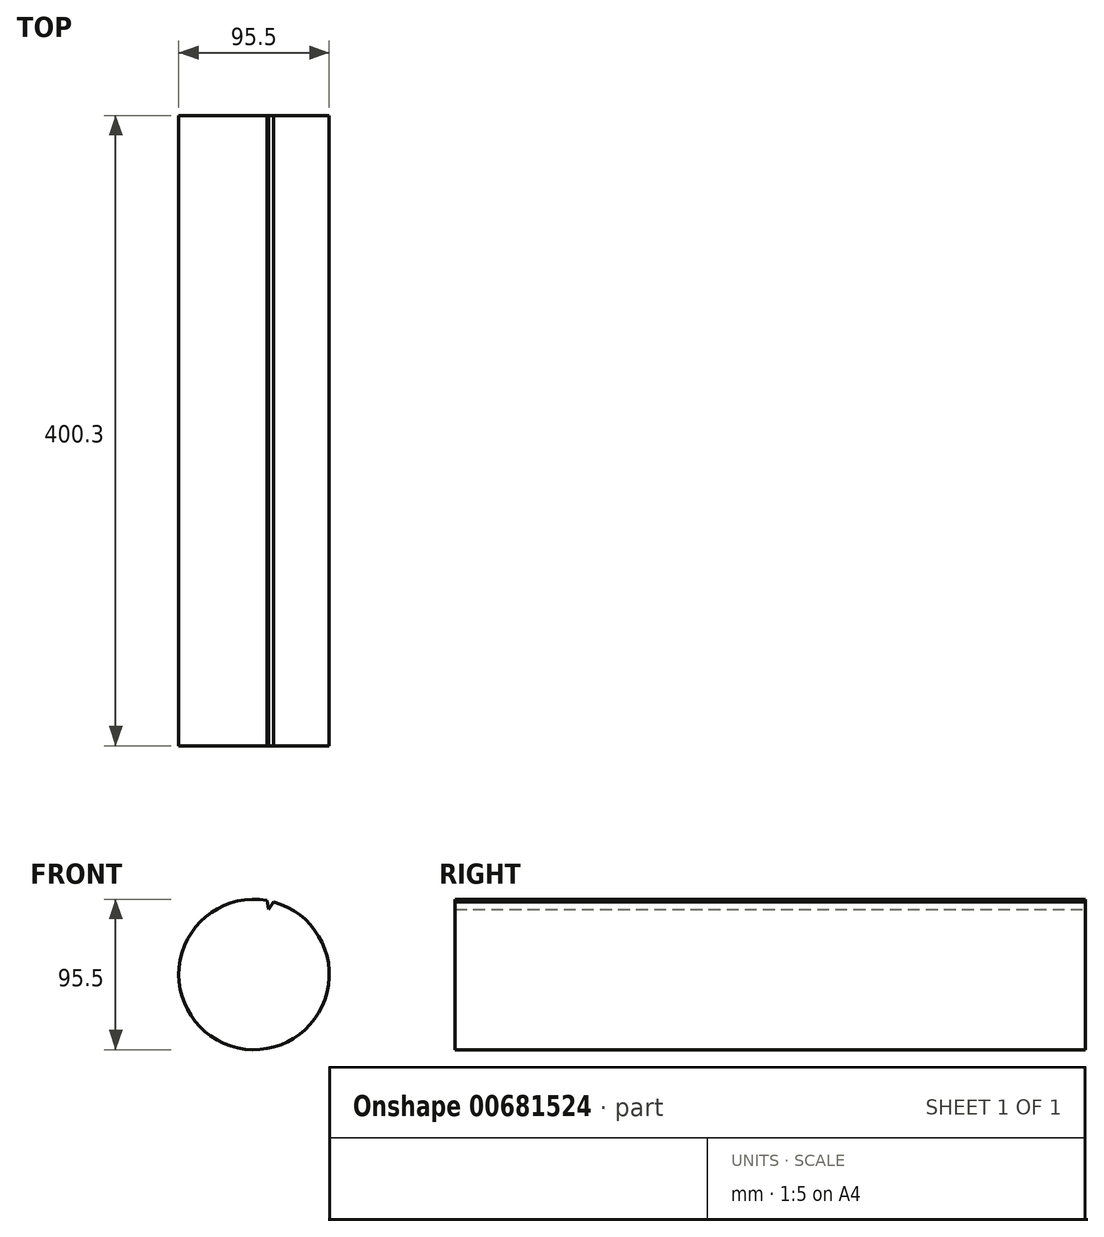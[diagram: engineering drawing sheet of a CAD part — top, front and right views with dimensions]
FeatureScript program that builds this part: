
annotation { "Feature Type Name" : "Feature", "Feature Type Description" : "" }
export const myFeature = defineFeature(function(context is Context, id is Id, definition is map)
    precondition{}
    {
        {
            var Q0;
            Q0=qCreatedBy(makeId("Front.planeOp"),FACE);
            var sketch = newSketch(context, id + "F0", { "sketchPlane" : qUnion([Q0])});
            skCircle(sketch, "E0", {"center": v(0, 0) * mm, "radius": 47.75 * mm});
            skSolve(sketch);
        }
        {
            var Q0;
            Q0=makeQuery(id+"F0.imprint","IMPRINT",FACE,{"disambiguationData":[TD([[makeQuery(id+"F0.imprint","IMPRINT",EDGE,{"derivedFrom":sQuery(id+"F0.wireOp",EDGE,"E0")}),1.0]])]});
            extrude(context, id + "F1", {"entities" : qUnion([Q0]), "depth" : 400.3 * mm, "offsetDistance" : 25.4 * mm});
        }
        {
            var Q0;
            Q0=makeQuery(id+"F1.opExtrude","CAP_FACE",FACE,{"disambiguationData":[OSD([sQuery(id+"F0.wireOp",EDGE,"E0")])],"isStart":true});
            var sketch = newSketch(context, id + "F2", { "sketchPlane" : qUnion([Q0])});
            skLineSegment(sketch, "E1", {"start": v(-6.71, 56.6) * mm, "end": v(-9.17, 41.4) * mm});
            skLineSegment(sketch, "E2", {"start": v(-9.17, 41.4) * mm, "end": v(-17.8, 54.13) * mm});
            skLineSegment(sketch, "E3", {"start": v(-17.8, 54.13) * mm, "end": v(-6.71, 56.6) * mm});
            skLineSegment(sketch, "E4", {"start": v(-12.26, 55.36) * mm, "end": v(0, 0) * mm, "construction": true});
            skSolve(sketch);
        }
        {
            var Q0;
            Q0 = qSketchRegion(id + "F2", true);
            extrude(context, id + "F3", {"entities" : qUnion([Q0]), "operationType" : NewBodyOperationType.REMOVE, "endBound" : BoundingType.THROUGH_ALL, "oppositeDirection" : true, "depth" : 25.4 * mm, "offsetDistance" : 25.4 * mm});
        }
    });
